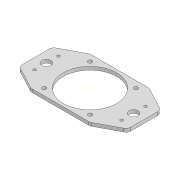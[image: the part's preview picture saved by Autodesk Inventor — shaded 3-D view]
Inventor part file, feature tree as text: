
AUTODESK INVENTOR PART (.ipt)
format: ipt  version: 2020 (Build 240168000, 168)  size: 151,552 bytes
history: native  units: mm
features: mirror x2, other x1, extrude x1, sketch x1
ambient origin geometry x8: Origin, YZ Plane, XZ Plane, XY Plane, X Axis, Y Axis, Z Axis, Center Point
bodies: Body1 (feature_tree)
feature tree (5):
  other  "Sólido1"
  extrude  "Extrusão1"  Depth=36.0mm
  mirror  "Espelhamento1"
  mirror  "Espelhamento3"
  sketch  "Esboço2"  dims[d0=65.0mm d1=36.0mm d2=36.0mm d4=5.0mm d5=4.0mm d6=0.0mm d9=11.0mm d10=17.1mm d11=3.5mm d12=14.5mm d13=20.0mm d14=6.0mm d15=6.0mm d16=30.181429mm]
